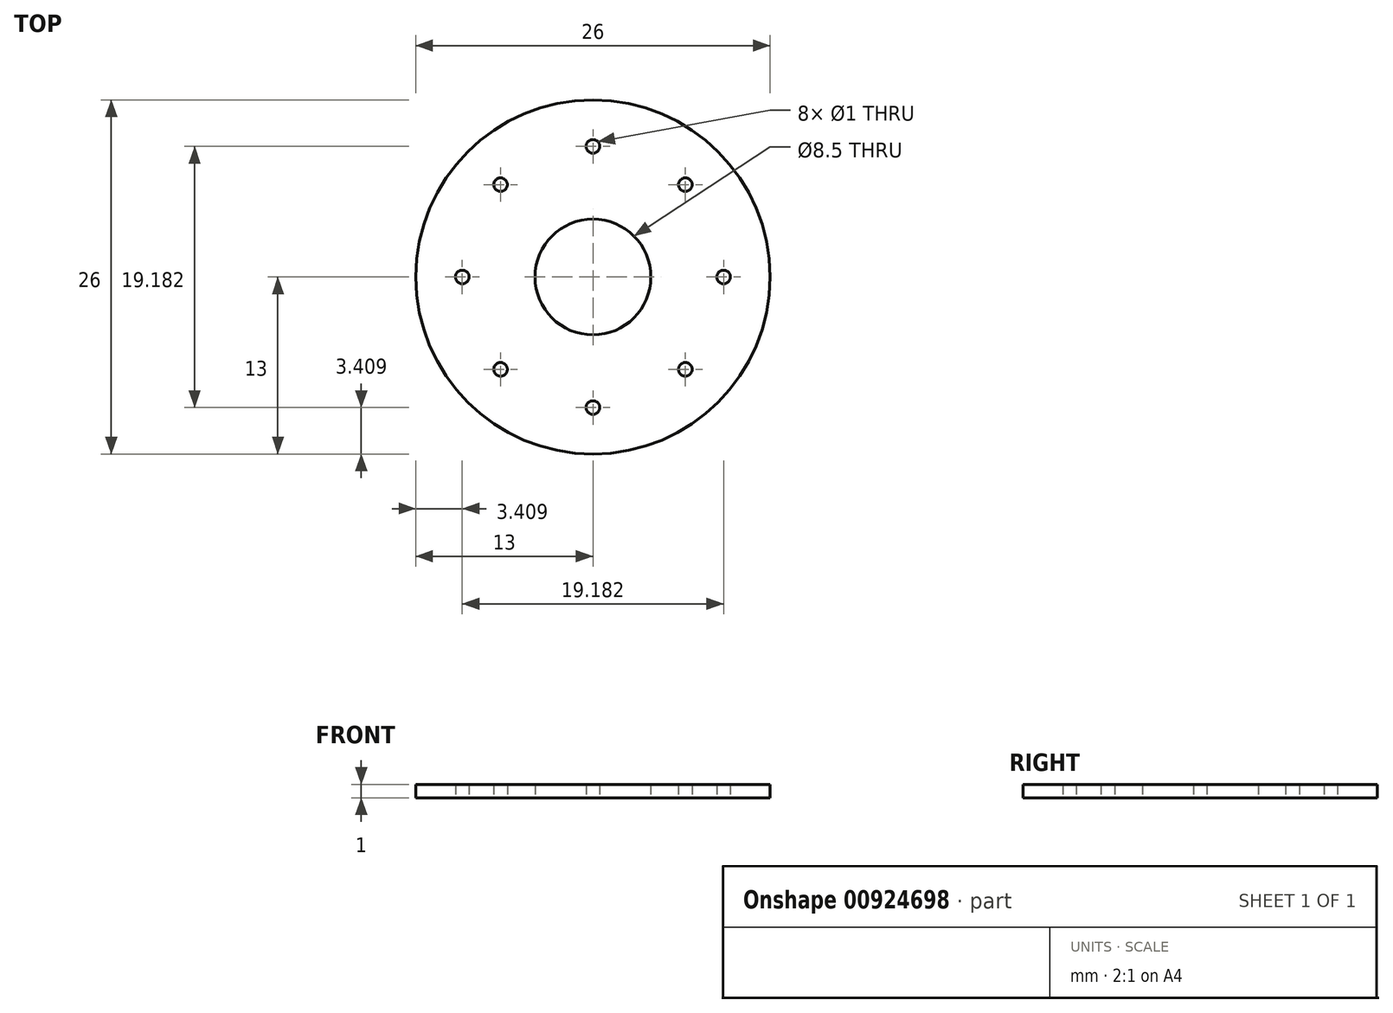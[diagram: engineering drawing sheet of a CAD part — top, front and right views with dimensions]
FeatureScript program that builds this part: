
annotation { "Feature Type Name" : "Feature", "Feature Type Description" : "" }
export const myFeature = defineFeature(function(context is Context, id is Id, definition is map)
    precondition{}
    {
        {
            var Q0;
            Q0=qCreatedBy(makeId("Top.planeOp"),FACE);
            var sketch = newSketch(context, id + "F0", { "sketchPlane" : qUnion([Q0])});
            skCircle(sketch, "E0", {"center": v(0, 0) * mm, "radius": 4.75 * mm, "construction": true});
            skCircle(sketch, "E1", {"center": v(0, 0) * mm, "radius": 9 * mm, "construction": true});
            skCircle(sketch, "E2", {"center": v(0, 0) * mm, "radius": 13 * mm});
            skCircle(sketch, "E3", {"center": v(0, 0) * mm, "radius": 4.25 * mm});
            skCircle(sketch, "E4", {"center": v(0, 9.6) * mm, "radius": 0.5 * mm});
            skCircle(sketch, "E5.1.0", {"center": v(-6.78, 6.78) * mm, "radius": 0.5 * mm});
            skCircle(sketch, "E5.2.0", {"center": v(-9.6, 0) * mm, "radius": 0.5 * mm});
            skCircle(sketch, "E5.3.0", {"center": v(-6.78, -6.78) * mm, "radius": 0.5 * mm});
            skCircle(sketch, "E5.4.0", {"center": v(0, -9.6) * mm, "radius": 0.5 * mm});
            skCircle(sketch, "E5.5.0", {"center": v(6.78, -6.78) * mm, "radius": 0.5 * mm});
            skCircle(sketch, "E5.6.0", {"center": v(9.6, 0) * mm, "radius": 0.5 * mm});
            skCircle(sketch, "E5.7.0", {"center": v(6.78, 6.78) * mm, "radius": 0.5 * mm});
            skSolve(sketch);
        }
        {
            var Q0;
            Q0=makeQuery(id+"F0.imprint","IMPRINT",FACE,{"disambiguationData":[TD([[makeQuery(id+"F0.imprint","IMPRINT",EDGE,{"derivedFrom":sQuery(id+"F0.wireOp",EDGE,"E2")}),1.0]])]});
            extrude(context, id + "F1", {"entities" : qUnion([Q0]), "depth" : 1 * mm, "offsetDistance" : 25 * mm});
        }
    });
